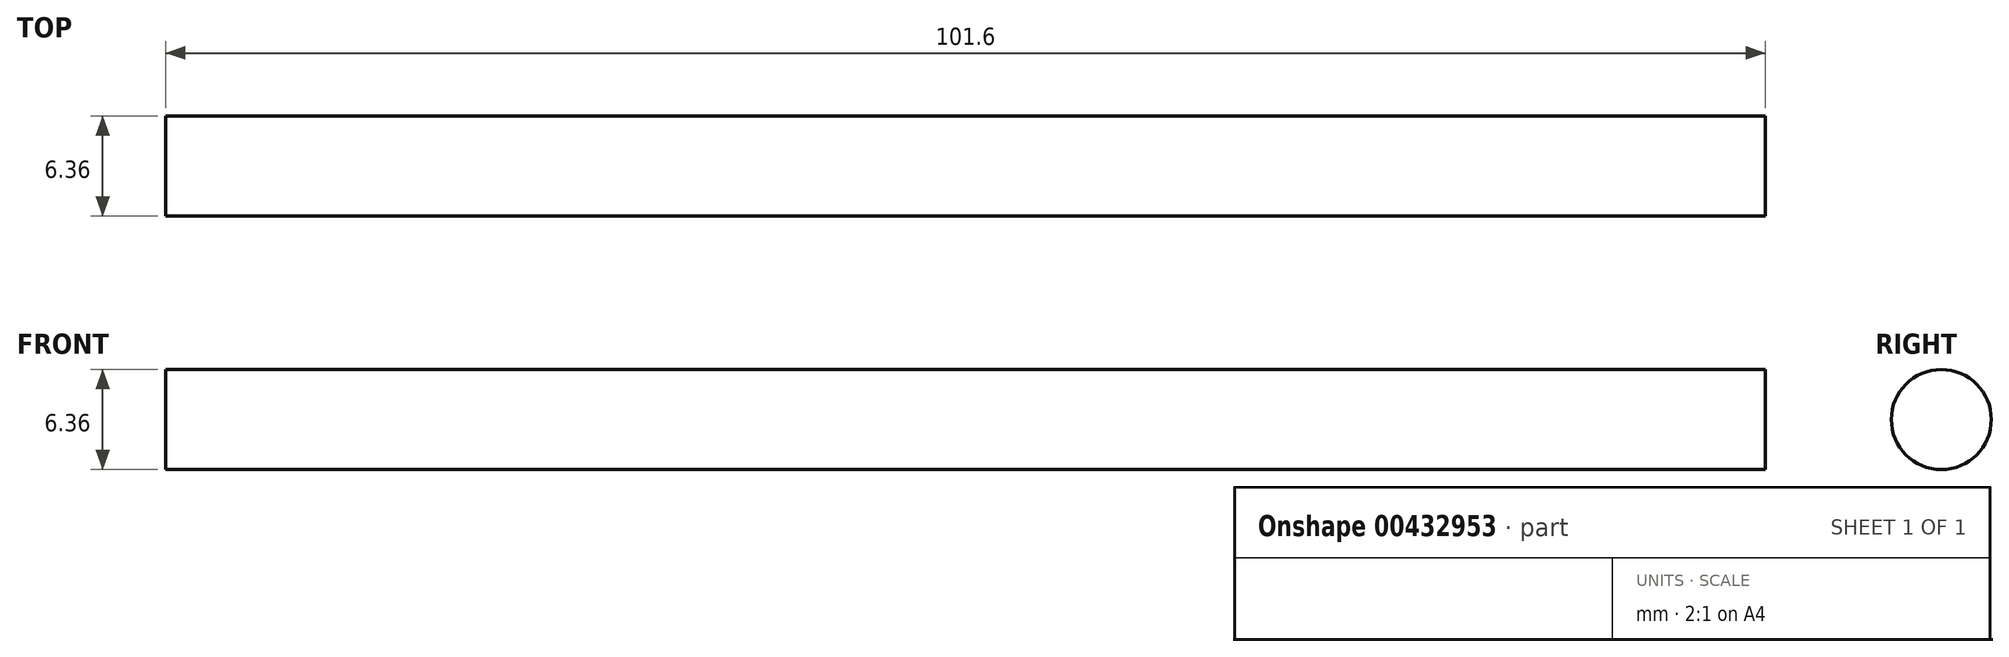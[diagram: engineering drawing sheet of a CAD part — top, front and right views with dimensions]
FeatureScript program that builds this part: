
annotation { "Feature Type Name" : "Feature", "Feature Type Description" : "" }
export const myFeature = defineFeature(function(context is Context, id is Id, definition is map)
    precondition{}
    {
        {
            var Q0;
            Q0=qCreatedBy(makeId("Right.planeOp"),FACE);
            var sketch = newSketch(context, id + "F0", { "sketchPlane" : qUnion([Q0])});
            skCircle(sketch, "E0", {"center": v(0, 0) * mm, "radius": 3.18 * mm});
            skSolve(sketch);
        }
        {
            var Q0;
            Q0 = qSketchRegion(id + "F0", true);
            extrude(context, id + "F1", {"entities" : qUnion([Q0]), "depth" : 101.6 * mm});
        }
    });
